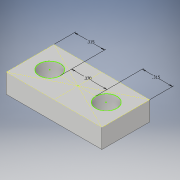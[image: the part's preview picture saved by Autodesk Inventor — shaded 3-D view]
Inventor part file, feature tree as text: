
AUTODESK INVENTOR PART (.ipt)
format: ipt  version: 2019 (Build 230136000, 136)  size: 125,440 bytes
history: native  units: in
note: dims shown in document units (in); Inventor stores cm internally (conversion verified against a paired STEP export)
features: extrude x2, other x2
ambient origin geometry x8: Origin, YZ Plane, XZ Plane, XY Plane, X Axis, Y Axis, Z Axis, Center Point
bodies: Solid1 (feature_tree)
feature tree (4):
  extrude  "Spacer Body"  Depth=0.2in TaperAngle=0.0deg
  other  "Spacer Circles"
  extrude  "Spacer Holes"  Depth=0.4in TaperAngle=0.0deg
  other  "Spacer 2D"
